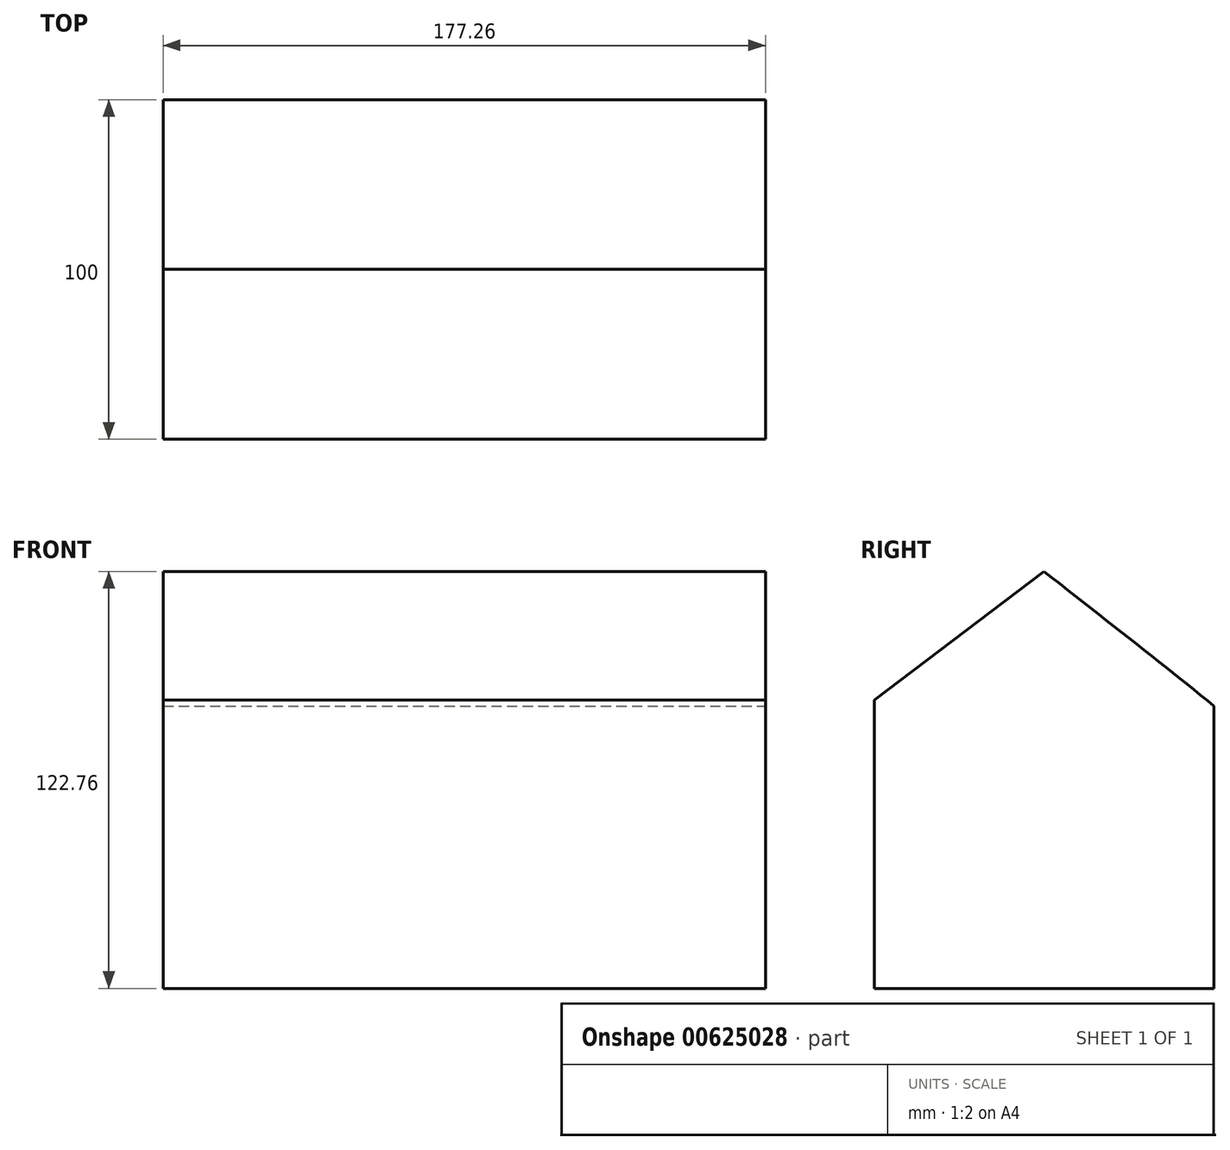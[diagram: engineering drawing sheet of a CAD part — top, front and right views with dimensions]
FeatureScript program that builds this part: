
annotation { "Feature Type Name" : "Feature", "Feature Type Description" : "" }
export const myFeature = defineFeature(function(context is Context, id is Id, definition is map)
    precondition{}
    {
        {
            var Q0;
            Q0=qCreatedBy(makeId("Front.planeOp"),FACE);
            var sketch = newSketch(context, id + "F0", { "sketchPlane" : qUnion([Q0])});
            skLineSegment(sketch, "E0.bottom", {"start": v(-88.63, -61.38) * mm, "end": v(88.63, -61.38) * mm});
            skLineSegment(sketch, "E0.top", {"start": v(-88.63, 61.38) * mm, "end": v(88.63, 61.38) * mm});
            skLineSegment(sketch, "E0.left", {"start": v(-88.63, -61.38) * mm, "end": v(-88.63, 61.38) * mm});
            skLineSegment(sketch, "E0.right", {"start": v(88.63, -61.38) * mm, "end": v(88.63, 61.38) * mm});
            skPoint(sketch, "E0.middle", {"position": v(0, 0) * mm});
            skSolve(sketch);
        }
        {
            var Q0;
            Q0=makeQuery(id+"F0.imprint","IMPRINT",FACE,{"disambiguationData":[TD([[makeQuery(id+"F0.imprint","IMPRINT",EDGE,{"derivedFrom":sQuery(id+"F0.wireOp",EDGE,"E0.bottom")}),1.0]])]});
            extrude(context, id + "F1", {"entities" : qUnion([Q0]), "endBound" : BoundingType.SYMMETRIC, "depth" : 100 * mm, "offsetDistance" : 25 * mm});
        }
        {
            var Q0;
            Q0=makeQuery(id+"F1.opExtrude","SWEPT_FACE",FACE,{"disambiguationData":[OSD([sQuery(id+"F0.wireOp",EDGE,"E0.right")])]});
            var sketch = newSketch(context, id + "F2", { "sketchPlane" : qUnion([Q0])});
            skFitSpline(sketch, "E1", {"points": [v(-61.38, 14.87) * mm, v(0, 61.38) * mm], "startDerivative": vector(61.38, 46.5) * mm, "endDerivative": vector(61.38, 46.5) * mm});
            skFitSpline(sketch, "E2", {"points": [v(0, 61.38) * mm, v(58.38, 14.87) * mm, v(88.13, -11.13) * mm], "startDerivative": vector(109.6, -85.73) * mm, "endDerivative": vector(64.28, -57.82) * mm});
            skSolve(sketch);
        }
        {
            var Q0;
            {var subQ0=sQuery(id+"F2.wireOp",EDGE,"E1");var subQ1=sQuery(id+"F0.wireOp",EDGE,"E0.right");var subQ4=makeQuery(id+"F1.opExtrude","CAP_EDGE",EDGE,{"disambiguationData":[OSD([subQ1])],"isStart":false});var subQ5=makeQuery(id+"F2.imprint","INTERSECT",VERTEX,{"derivedFrom":[subQ4,subQ0]});Q0=makeQuery(id+"F2.imprint","IMPRINT",FACE,{"disambiguationData":[TD([[makeQuery(id+"F2.imprint","IMPRINT",EDGE,{"disambiguationData":[TD([[subQ5,-1.0]])],"derivedFrom":subQ4}),-1.0]])]});}
            var Q1;
            {var subQ0=sQuery(id+"F2.wireOp",EDGE,"E2");var subQ1=sQuery(id+"F0.wireOp",EDGE,"E0.right");var subQ4=makeQuery(id+"F1.opExtrude","CAP_EDGE",EDGE,{"disambiguationData":[OSD([subQ1])],"isStart":true});var subQ5=makeQuery(id+"F2.imprint","INTERSECT",VERTEX,{"derivedFrom":[subQ4,subQ0]});Q1=makeQuery(id+"F2.imprint","IMPRINT",FACE,{"disambiguationData":[TD([[makeQuery(id+"F2.imprint","IMPRINT",EDGE,{"disambiguationData":[TD([[subQ5,-1.0]])],"derivedFrom":subQ4}),1.0]])]});}
            extrude(context, id + "F3", {"entities" : qUnion([Q0, Q1]), "operationType" : NewBodyOperationType.REMOVE, "oppositeDirection" : true, "depth" : 281.4 * mm, "offsetDistance" : 25 * mm});
        }
    });
